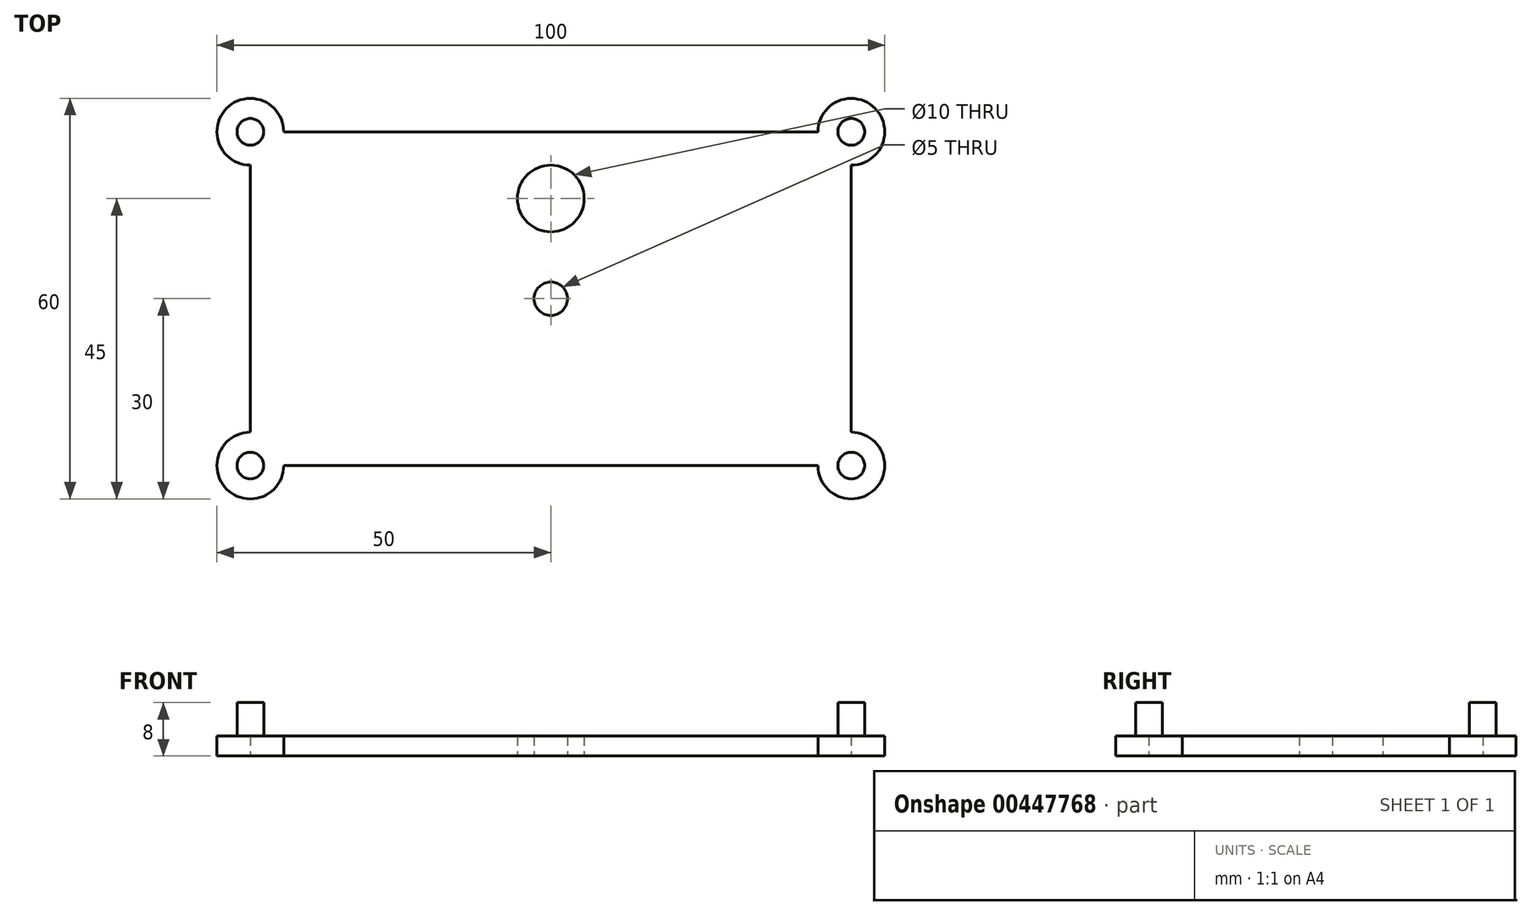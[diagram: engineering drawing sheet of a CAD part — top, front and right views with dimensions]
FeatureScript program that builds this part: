
annotation { "Feature Type Name" : "Feature", "Feature Type Description" : "" }
export const myFeature = defineFeature(function(context is Context, id is Id, definition is map)
    precondition{}
    {
        {
            var Q0;
            Q0=qCreatedBy(makeId("Top.planeOp"),FACE);
            var sketch = newSketch(context, id + "F0", { "sketchPlane" : qUnion([Q0])});
            skLineSegment(sketch, "E0.bottom", {"start": v(-40, 25) * mm, "end": v(40, 25) * mm});
            skLineSegment(sketch, "E0.top", {"start": v(-40, -25) * mm, "end": v(40, -25) * mm});
            skLineSegment(sketch, "E0.left", {"start": v(-45, 20) * mm, "end": v(-45, -20) * mm});
            skLineSegment(sketch, "E0.right", {"start": v(45, 20) * mm, "end": v(45, -20) * mm});
            skPoint(sketch, "E0.middle", {"position": v(0, 0) * mm});
            skArc(sketch, "E1", {"start": v(-40, 25) * mm, "mid": v(-48.54, 28.54) * mm, "end": v(-45, 20) * mm});
            skArc(sketch, "E2", {"start": v(45, 20) * mm, "mid": v(48.54, 28.54) * mm, "end": v(40, 25) * mm});
            skArc(sketch, "E3", {"start": v(40, -25) * mm, "mid": v(48.54, -28.54) * mm, "end": v(45, -20) * mm});
            skArc(sketch, "E4", {"start": v(-45, -20) * mm, "mid": v(-48.54, -28.54) * mm, "end": v(-40, -25) * mm});
            skCircle(sketch, "E5", {"center": v(-45, 25) * mm, "radius": 2 * mm});
            skCircle(sketch, "E6", {"center": v(45, 25) * mm, "radius": 2 * mm});
            skCircle(sketch, "E7", {"center": v(45, -25) * mm, "radius": 2 * mm});
            skCircle(sketch, "E8", {"center": v(-45, -25) * mm, "radius": 2 * mm});
            skSolve(sketch);
        }
        {
            var Q0;
            Q0=makeQuery(id+"F0.imprint","IMPRINT",FACE,{"disambiguationData":[TD([[makeQuery(id+"F0.imprint","IMPRINT",EDGE,{"derivedFrom":sQuery(id+"F0.wireOp",EDGE,"E0.bottom")}),-1.0]])]});
            extrude(context, id + "F1", {"entities" : qUnion([Q0]), "depth" : 3 * mm});
        }
        {
            var Q0;
            Q0=makeQuery(id+"F0.imprint","IMPRINT",FACE,{"disambiguationData":[TD([[makeQuery(id+"F0.imprint","IMPRINT",EDGE,{"derivedFrom":sQuery(id+"F0.wireOp",EDGE,"E8")}),1.0]])]});
            var Q1;
            Q1=makeQuery(id+"F0.imprint","IMPRINT",FACE,{"disambiguationData":[TD([[makeQuery(id+"F0.imprint","IMPRINT",EDGE,{"derivedFrom":sQuery(id+"F0.wireOp",EDGE,"E7")}),1.0]])]});
            var Q2;
            Q2=makeQuery(id+"F0.imprint","IMPRINT",FACE,{"disambiguationData":[TD([[makeQuery(id+"F0.imprint","IMPRINT",EDGE,{"derivedFrom":sQuery(id+"F0.wireOp",EDGE,"E6")}),1.0]])]});
            var Q3;
            Q3=makeQuery(id+"F0.imprint","IMPRINT",FACE,{"disambiguationData":[TD([[makeQuery(id+"F0.imprint","IMPRINT",EDGE,{"derivedFrom":sQuery(id+"F0.wireOp",EDGE,"E5")}),1.0]])]});
            extrude(context, id + "F2", {"entities" : qUnion([Q0, Q1, Q2, Q3]), "operationType" : NewBodyOperationType.ADD, "depth" : 8 * mm});
        }
        {
            var Q0;
            Q0=qCreatedBy(makeId("Top.planeOp"),FACE);
            var sketch = newSketch(context, id + "F3", { "sketchPlane" : qUnion([Q0])});
            skLineSegment(sketch, "E9", {"start": v(0, 0) * mm, "end": v(0, 15) * mm});
            skCircle(sketch, "E10", {"center": v(0, 15) * mm, "radius": 5 * mm});
            skCircle(sketch, "E11", {"center": v(0, 0) * mm, "radius": 2.5 * mm});
            skSolve(sketch);
        }
        {
            var Q0;
            Q0=makeQuery(id+"F3.imprint","IMPRINT",FACE,{"disambiguationData":[TD([[makeQuery(id+"F3.imprint","IMPRINT",EDGE,{"derivedFrom":sQuery(id+"F3.wireOp",EDGE,"E11")}),1.0]])]});
            var Q1;
            Q1=makeQuery(id+"F3.imprint","IMPRINT",FACE,{"disambiguationData":[TD([[makeQuery(id+"F3.imprint","IMPRINT",EDGE,{"derivedFrom":sQuery(id+"F3.wireOp",EDGE,"E10")}),1.0]])]});
            extrude(context, id + "F4", {"entities" : qUnion([Q0, Q1]), "operationType" : NewBodyOperationType.REMOVE, "depth" : 4 * mm});
        }
    });
